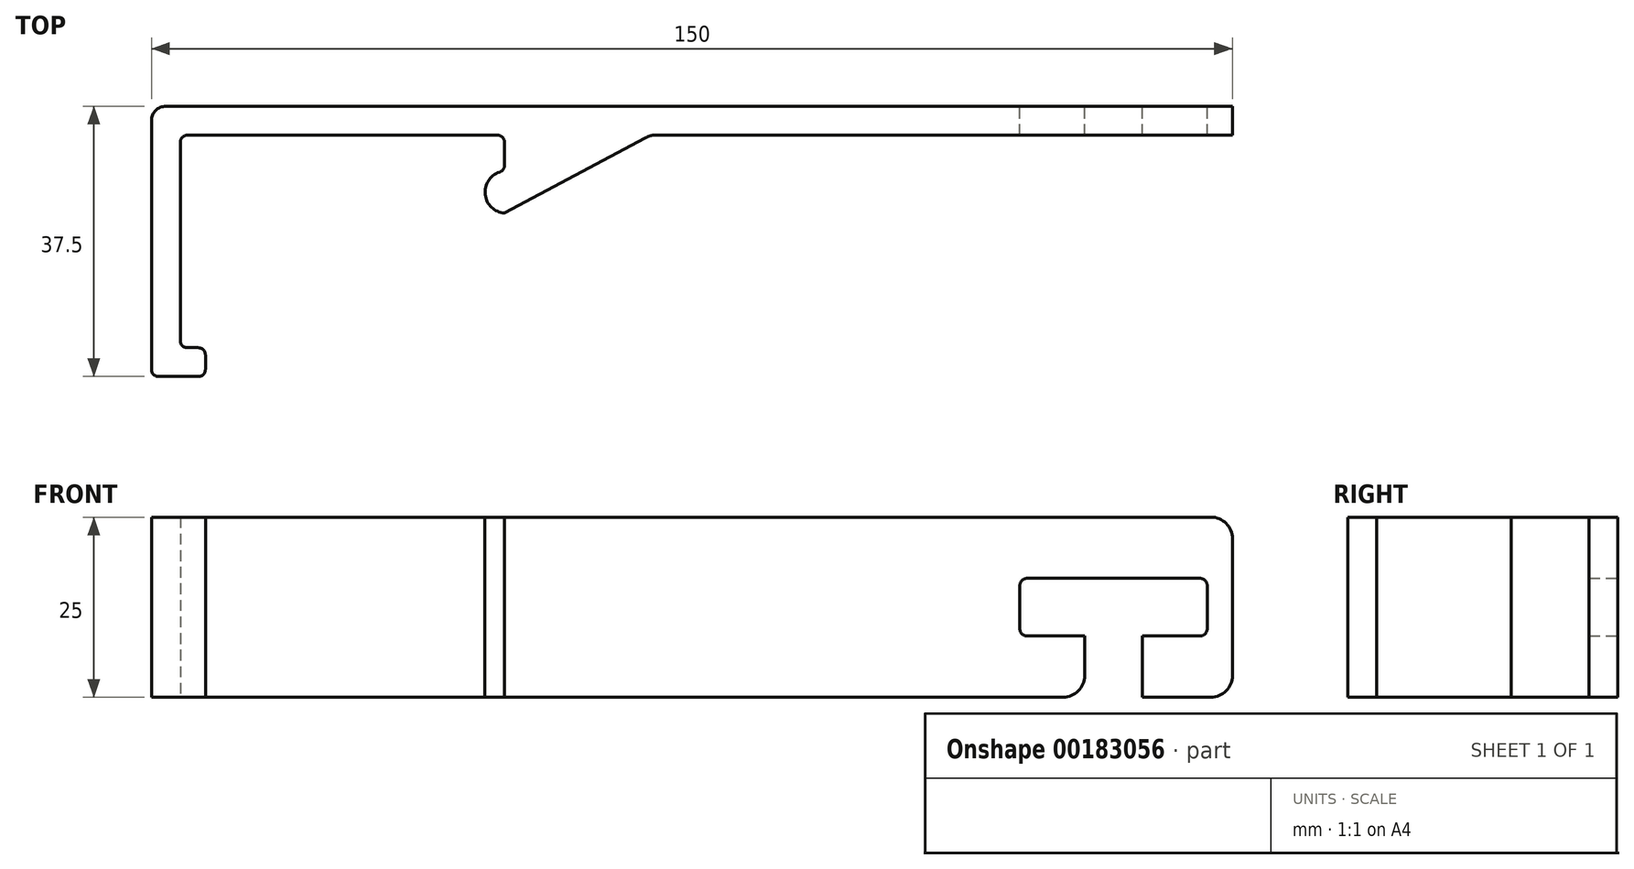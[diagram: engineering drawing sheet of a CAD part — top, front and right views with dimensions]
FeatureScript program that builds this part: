
annotation { "Feature Type Name" : "Feature", "Feature Type Description" : "" }
export const myFeature = defineFeature(function(context is Context, id is Id, definition is map)
    precondition{}
    {
        {
            var Q0;
            Q0=qCreatedBy(makeId("Top.planeOp"),FACE);
            var sketch = newSketch(context, id + "F0", { "sketchPlane" : qUnion([Q0])});
            skLineSegment(sketch, "E0", {"start": v(-61.73, -27.88) * mm, "end": v(-69.22, -27.88) * mm});
            skLineSegment(sketch, "E1", {"start": v(-69.22, -27.88) * mm, "end": v(-69.22, 9.62) * mm});
            skLineSegment(sketch, "E2", {"start": v(-69.22, 9.62) * mm, "end": v(80.78, 9.62) * mm});
            skLineSegment(sketch, "E3", {"start": v(80.78, 9.62) * mm, "end": v(80.78, 5.62) * mm});
            skLineSegment(sketch, "E4", {"start": v(80.78, 5.62) * mm, "end": v(0, 5.62) * mm});
            skLineSegment(sketch, "E5", {"start": v(0, 5.62) * mm, "end": v(-20.22, -5.2) * mm});
            skLineSegment(sketch, "E6", {"start": v(-20.22, 5.62) * mm, "end": v(-65.22, 5.62) * mm});
            skLineSegment(sketch, "E7", {"start": v(-65.22, 5.62) * mm, "end": v(-65.22, -23.88) * mm});
            skLineSegment(sketch, "E8", {"start": v(-65.22, -23.88) * mm, "end": v(-61.73, -23.88) * mm});
            skLineSegment(sketch, "E9", {"start": v(-61.73, -23.88) * mm, "end": v(-61.73, -27.88) * mm});
            skLineSegment(sketch, "E10", {"start": v(-20.22, 0.62) * mm, "end": v(-20.22, 5.62) * mm});
            skArc(sketch, "E11", {"start": v(-20.22, 0.62) * mm, "mid": v(-22.94, -2.3) * mm, "end": v(-20.22, -5.2) * mm});
            skSolve(sketch);
        }
        {
            var Q0;
            Q0 = qSketchRegion(id + "F0", true);
            extrude(context, id + "F1", {"entities" : qUnion([Q0]), "depth" : 25 * mm});
        }
        {
            var Q0;
            Q0=makeQuery(id+"F1.opExtrude","SWEPT_FACE",FACE,{"disambiguationData":[OSD([sQuery(id+"F0.wireOp",EDGE,"E2")])]});
            var sketch = newSketch(context, id + "F2", { "sketchPlane" : qUnion([Q0])});
            skLineSegment(sketch, "E12", {"start": v(-68.28, 0) * mm, "end": v(-68.28, 8.5) * mm});
            skLineSegment(sketch, "E13", {"start": v(-68.28, 8.5) * mm, "end": v(-77.28, 8.5) * mm});
            skLineSegment(sketch, "E14", {"start": v(-77.28, 8.5) * mm, "end": v(-77.28, 16.5) * mm});
            skLineSegment(sketch, "E15", {"start": v(-77.28, 16.5) * mm, "end": v(-51.28, 16.5) * mm});
            skLineSegment(sketch, "E16", {"start": v(-51.28, 16.5) * mm, "end": v(-51.28, 8.5) * mm});
            skLineSegment(sketch, "E17", {"start": v(-51.28, 8.5) * mm, "end": v(-60.28, 8.5) * mm});
            skLineSegment(sketch, "E18", {"start": v(-60.28, 8.5) * mm, "end": v(-60.28, 0) * mm});
            skLineSegment(sketch, "E19", {"start": v(-60.28, 0) * mm, "end": v(-68.28, 0) * mm});
            skSolve(sketch);
        }
        {
            var Q0;
            Q0 = qSketchRegion(id + "F2", true);
            extrude(context, id + "F3", {"entities" : qUnion([Q0]), "operationType" : NewBodyOperationType.REMOVE, "endBound" : BoundingType.THROUGH_ALL, "oppositeDirection" : true, "depth" : 25 * mm});
        }
        {
            var Q0;
            Q0=makeQuery(id+"F3.boolean.opBoolean","COPY",EDGE,{"derivedFrom":makeQuery(id+"F3.opExtrude","SWEPT_EDGE",EDGE,{"disambiguationData":[OSD([sQuery(id+"F2.wireOp",EDGE,"E14"),sQuery(id+"F2.wireOp",EDGE,"E15")])]})});
            var Q1;
            Q1=makeQuery(id+"F3.boolean.opBoolean","COPY",EDGE,{"derivedFrom":makeQuery(id+"F3.opExtrude","SWEPT_EDGE",EDGE,{"disambiguationData":[OSD([sQuery(id+"F2.wireOp",EDGE,"E13"),sQuery(id+"F2.wireOp",EDGE,"E14")])]})});
            var Q2;
            Q2=makeQuery(id+"F3.boolean.opBoolean","COPY",EDGE,{"derivedFrom":makeQuery(id+"F3.opExtrude","SWEPT_EDGE",EDGE,{"disambiguationData":[OSD([sQuery(id+"F2.wireOp",EDGE,"E15"),sQuery(id+"F2.wireOp",EDGE,"E16")])]})});
            var Q3;
            Q3=makeQuery(id+"F3.boolean.opBoolean","COPY",EDGE,{"derivedFrom":makeQuery(id+"F3.opExtrude","SWEPT_EDGE",EDGE,{"disambiguationData":[OSD([sQuery(id+"F2.wireOp",EDGE,"E16"),sQuery(id+"F2.wireOp",EDGE,"E17")])]})});
            var Q4;
            Q4=makeQuery(id+"F1.opExtrude","SWEPT_EDGE",EDGE,{"disambiguationData":[OSD([sQuery(id+"F0.wireOp",EDGE,"E6"),sQuery(id+"F0.wireOp",EDGE,"E7")])]});
            var Q5;
            Q5=makeQuery(id+"F1.opExtrude","SWEPT_EDGE",EDGE,{"disambiguationData":[OSD([sQuery(id+"F0.wireOp",EDGE,"E6"),sQuery(id+"F0.wireOp",EDGE,"E10")])]});
            var Q6;
            Q6=makeQuery(id+"F1.opExtrude","SWEPT_EDGE",EDGE,{"disambiguationData":[OSD([sQuery(id+"F0.wireOp",EDGE,"E10"),sQuery(id+"F0.wireOp",EDGE,"E11")])]});
            var Q7;
            Q7=makeQuery(id+"F1.opExtrude","SWEPT_EDGE",EDGE,{"disambiguationData":[OSD([sQuery(id+"F0.wireOp",EDGE,"E7"),sQuery(id+"F0.wireOp",EDGE,"E8")])]});
            var Q8;
            Q8=makeQuery(id+"F1.opExtrude","SWEPT_EDGE",EDGE,{"disambiguationData":[OSD([sQuery(id+"F0.wireOp",EDGE,"E8"),sQuery(id+"F0.wireOp",EDGE,"E9")])]});
            var Q9;
            Q9=makeQuery(id+"F1.opExtrude","SWEPT_EDGE",EDGE,{"disambiguationData":[OSD([sQuery(id+"F0.wireOp",EDGE,"E0"),sQuery(id+"F0.wireOp",EDGE,"E9")])]});
            var Q10;
            Q10=makeQuery(id+"F1.opExtrude","SWEPT_EDGE",EDGE,{"disambiguationData":[OSD([sQuery(id+"F0.wireOp",EDGE,"E0"),sQuery(id+"F0.wireOp",EDGE,"E1")])]});
            fillet(context, id + "F4", {"entities" : qUnion([Q0, Q1, Q2, Q3, Q4, Q5, Q6, Q7, Q8, Q9, Q10]), "radius" : 1 * mm, "tangentPropagation" : true, "allowEdgeOverflow" : false});
        }
        {
            var Q0;
            Q0=makeQuery(id+"F1.opExtrude","CAP_EDGE",EDGE,{"disambiguationData":[OSD([sQuery(id+"F0.wireOp",EDGE,"E3")])],"isStart":true});
            var Q1;
            Q1=makeQuery(id+"F1.opExtrude","CAP_EDGE",EDGE,{"disambiguationData":[OSD([sQuery(id+"F0.wireOp",EDGE,"E3")])],"isStart":false});
            var Q2;
            Q2=makeQuery(id+"F3.boolean.opBoolean","COPY",EDGE,{"derivedFrom":makeQuery(id+"F3.opExtrude","SWEPT_EDGE",EDGE,{"disambiguationData":[OSD([sQuery(id+"F0.wireOp",EDGE,"E2"),sQuery(id+"F2.wireOp",EDGE,"E12"),sQuery(id+"F2.wireOp",EDGE,"E19")])]})});
            var Q3;
            Q3=makeQuery(id+"F3.boolean.opBoolean","COPY",EDGE,{"derivedFrom":makeQuery(id+"F3.opExtrude","SWEPT_EDGE",EDGE,{"disambiguationData":[OSD([sQuery(id+"F0.wireOp",EDGE,"E2"),sQuery(id+"F2.wireOp",EDGE,"E18"),sQuery(id+"F2.wireOp",EDGE,"E19")])]})});
            var Q4;
            Q4=makeQuery(id+"F1.opExtrude","SWEPT_EDGE",EDGE,{"disambiguationData":[OSD([sQuery(id+"F0.wireOp",EDGE,"E4"),sQuery(id+"F0.wireOp",EDGE,"E5")])]});
            fillet(context, id + "F5", {"entities" : qUnion([Q0, Q1, Q2, Q3, Q4]), "radius" : 3 * mm, "tangentPropagation" : true, "allowEdgeOverflow" : false});
        }
        {
            var Q0;
            Q0=makeQuery(id+"F1.opExtrude","SWEPT_EDGE",EDGE,{"disambiguationData":[OSD([sQuery(id+"F0.wireOp",EDGE,"E1"),sQuery(id+"F0.wireOp",EDGE,"E2")])]});
            fillet(context, id + "F6", {"entities" : qUnion([Q0]), "radius" : 2 * mm, "tangentPropagation" : true, "allowEdgeOverflow" : false});
        }
    });
